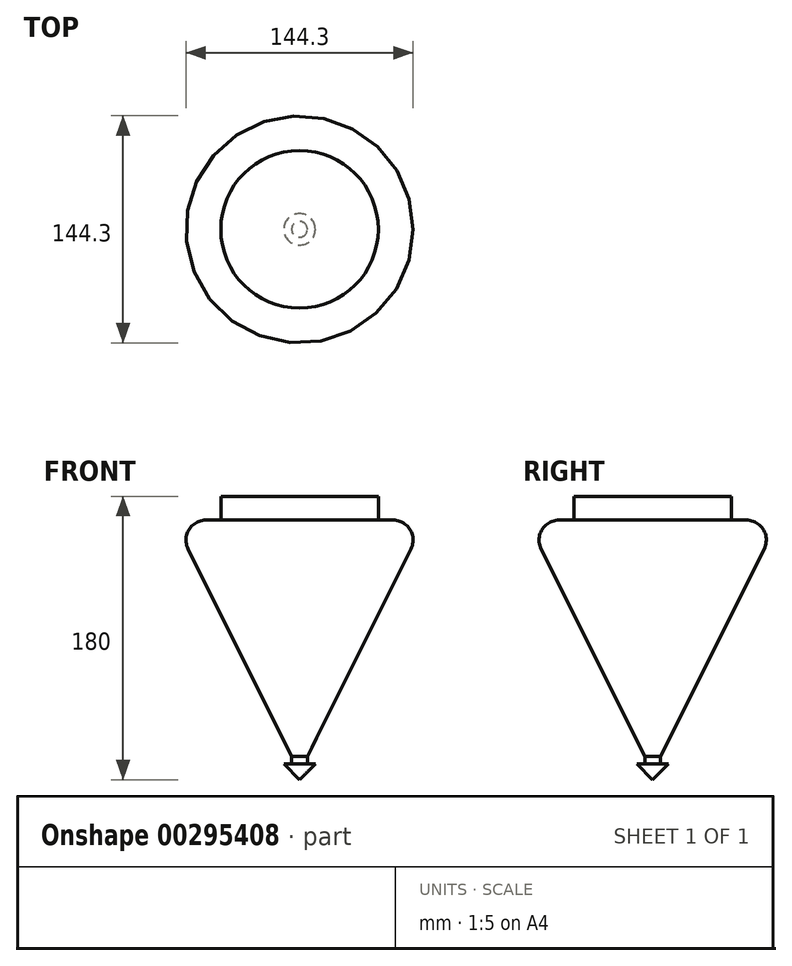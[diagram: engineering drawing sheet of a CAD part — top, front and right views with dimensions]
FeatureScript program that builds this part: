
annotation { "Feature Type Name" : "Feature", "Feature Type Description" : "" }
export const myFeature = defineFeature(function(context is Context, id is Id, definition is map)
    precondition{}
    {
        {
            var Q0;
            Q0=qCreatedBy(makeId("Front.planeOp"),FACE);
            var sketch = newSketch(context, id + "F0", { "sketchPlane" : qUnion([Q0])});
            skLineSegment(sketch, "E0", {"start": v(0, 0) * mm, "end": v(50, 0) * mm, "construction": true});
            skLineSegment(sketch, "E1", {"start": v(50, 0) * mm, "end": v(50, -15) * mm});
            skLineSegment(sketch, "E2", {"start": v(50, -15) * mm, "end": v(59.45, -15) * mm});
            skLineSegment(sketch, "E3", {"start": v(5, -165) * mm, "end": v(5, 0) * mm, "construction": true});
            skLineSegment(sketch, "E4", {"start": v(5, -165) * mm, "end": v(5, -170) * mm});
            skLineSegment(sketch, "E5", {"start": v(5, -170) * mm, "end": v(10, -170) * mm});
            skLineSegment(sketch, "E6", {"start": v(0, -180) * mm, "end": v(10, -170) * mm});
            skLineSegment(sketch, "E7", {"start": v(70.81, -33.38) * mm, "end": v(5, -165) * mm});
            skLineSegment(sketch, "E8", {"start": v(50, 0) * mm, "end": v(0, 0) * mm});
            skLineSegment(sketch, "E9", {"start": v(0, 0) * mm, "end": v(0, -180) * mm});
            skPoint(sketch, "E10.visualSharp", {"position": v(80, -15) * mm});
            skArc(sketch, "E10.filletArc", {"start": v(70.81, -33.38) * mm, "mid": v(70.25, -21.02) * mm, "end": v(59.45, -15) * mm});
            skSolve(sketch);
        }
        {
            var Q0;
            Q0=makeQuery(id+"F0.imprint","IMPRINT",FACE,{"disambiguationData":[TD([[makeQuery(id+"F0.imprint","IMPRINT",EDGE,{"derivedFrom":sQuery(id+"F0.wireOp",EDGE,"E1")}),-1.0]])]});
            var Q1;
            Q1=sQuery(id+"F0.wireOp",EDGE,"E9");
            revolve(context, id + "F1", {"entities" : qUnion([Q0]), "axis" : qUnion([Q1]), "revolveType" : RevolveType.FULL});
        }
    });
